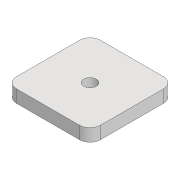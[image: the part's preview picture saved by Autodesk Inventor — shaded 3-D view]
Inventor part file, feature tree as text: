
AUTODESK INVENTOR PART (.ipt)
format: ipt  version: 2020 (Build 240168000, 168)  size: 89,600 bytes
history: native  units: mm
features: other x1, extrude x1, fillet x1, sketch x1
ambient origin geometry x8: Origin, YZ Plane, XZ Plane, XY Plane, X Axis, Y Axis, Z Axis, Center Point
bodies: Body1 (feature_tree)
feature tree (4):
  other  "Sólido1"
  extrude  "Extrusão1"  Depth=80.0mm
  fillet  "Arredondamento1"  Radius=12.0mm
  sketch  "Esboço1"  dims[d0=80.0mm d1=80.0mm d2=12.0mm d3=12.0mm d4=0.0mm d5=10.0mm]
